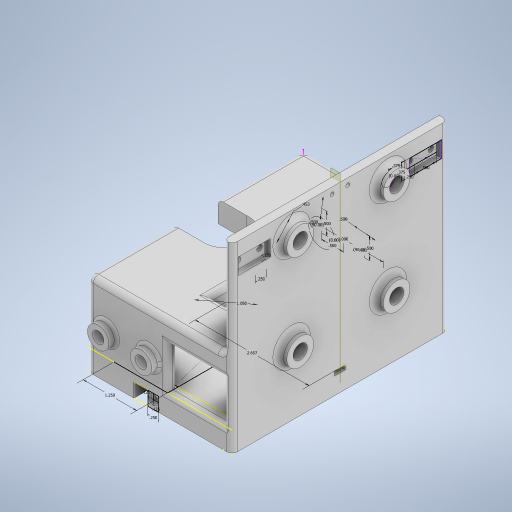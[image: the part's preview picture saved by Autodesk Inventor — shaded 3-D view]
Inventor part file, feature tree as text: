
AUTODESK INVENTOR PART (.ipt)
format: ipt  version: 2024.1 (Build 281209000, 209)  size: 974,336 bytes
history: native  units: in
note: dims shown in document units (in); Inventor stores cm internally (conversion verified against a paired STEP export)
features: extrude x22, sketch x15, hole x8, fillet x5, mirror x2, plane x1
ambient origin geometry x8: Origin, YZ Plane, XZ Plane, XY Plane, X Axis, Y Axis, Z Axis, Center Point
bodies: Solid1 (feature_tree)
feature tree (53):
  extrude  "Extrusion1"  Depth=3.3654in
  extrude  "Extrusion2"  Depth=0.375in
  extrude  "Extrusion3"  Depth=0.5in
  extrude  "Extrusion4"  Depth=4.5472in
  extrude  "Extrusion5"  Depth=0.25in
  extrude  "Extrusion6"  Depth=2.6575in
  hole  "Hole2"  [1 undecoded]
  extrude  "Extrusion7"  Depth=0.5in
  extrude  "Extrusion8"  Depth=1.5in
  extrude  "Extrusion9"  Depth=0.312in
  extrude  "Extrusion10"  Depth=0.312in
  hole  "Hole3"  [1 undecoded]
  extrude  "Extrusion11"  Depth=1.5in TaperAngle=0.0deg
  extrude  "Extrusion12"  Depth=1.125in
  hole  "Hole4"  [1 undecoded]
  sketch  "Sketch17"  dims[d34=1.4685in d35=0.0in d36=0.5in]
  extrude  "Extrusion13"  Depth=0.0625in
  hole  "Hole5"  [1 undecoded]
  plane  "Work Plane1"
  mirror  "Mirror1"
  extrude  "Extrusion14"  Depth=0.0625in
  fillet  "Fillet1"  [1 undecoded]
  extrude  "Extrusion15"  TaperAngle=0.0deg  [1 undecoded]
  fillet  "Fillet2"  Radius=0.625in
  hole  "Hole6"  [1 undecoded]
  mirror  "Mirror2"
  fillet  "Fillet3"  Radius=0.625in
  hole  "Hole7"  [1 undecoded]
  sketch  "Sketch22"  dims[d37=5.03in d38=0.0in d39=1.5in]
  extrude  "Extrusion16"  Depth=0.0625in TaperAngle=0.0deg
  fillet  "Fillet4"  Radius=0.36in
  sketch  "Sketch Driven Pattern1"  dims[d0=3.3654in d1=5.0299in]
  extrude  "Extrusion17"  Depth=0.0625in
  sketch  "Sketch24"  dims[d43=0.0in d44=0.312in]
  extrude  "Extrusion18"  Depth=0.0625in
  extrude  "Extrusion19"  Depth=0.0625in
  sketch  "Sketch26"  dims[d54=1.9685in d55=0.0in d56=1.5in d57=0.0in]
  extrude  "Extrusion20"  Depth=0.375in
  hole  "Hole8"  [1 undecoded]
  fillet  "Fillet5"  Radius=0.25in
  extrude  "Extrusion21"  Depth=0.5in
  sketch  "Sketch28"  dims[d61=1.49in d62=2.25in d63=2.25in d64=90.0deg d65=2.25in d66=90.0deg d67=0.332in d68=0.375in d69=0.119in d70=0.25in d71=0.5635in d72=0.375in d73=0.0in d74=0.0in d75=0.0in d76=0.625in d77=0.625in d78=0.625in d79=0.625in d80=0.2in d81=0.0in d82=0.36in d83=1.125in d84=0.185in d85=0.37in d86=0.09in d87=0.375in d88=0.119in d89=0.25in d90=0.5635in d91=0.375in d92=0.0in d93=0.375in d94=0.0in d95=0.25in d96=0.5in d97=0.375in d98=0.125in d99=0.0in d100=0.129in d101=0.198in d102=0.225in d103=0.188in d104=0.5635in d105=0.375in d106=0.0in d107=0.125in d108=0.125in d109=1.0in d110=1.0in d111=0.5in d112=1.5in d113=0.0in d114=0.931in d115=0.5in d116=1.0in d117=0.0in d120=0.1875in d121=0.0in d122=0.0625in d123=0.266in d124=0.75in d125=0.438in d126=0.25in d127=0.5635in d128=0.25in d129=0.0in d130=0.5in d131=90.0deg d132=0.5in d133=90.0deg d134=0.5in d135=0.5in d136=0.0625in d137=1.0in d138=0.5in d139=0.5in d140=90.0deg d141=0.5in d142=1.0in d143=180.0deg d144=1.0in d145=90.0deg d146=1.0in d147=0.266in d148=0.75in d149=0.438in d150=0.25in d151=0.5635in d152=1.0in d153=0.8108in d154=0.4532in d155=0.125in d156=0.0in d157=0.0312in d158=0.325in d159=0.1329in d160=0.3516in d161=0.1329in d162=0.3516in d163=0.448in d164=0.0in d165=0.647in d166=0.0in d167=0.325in d168=0.325in d169=0.25in d170=0.25in d171=0.5in d172=0.0in d173=0.25in d174=0.125in d175=0.0in d176=0.125in d177=0.129in d178=0.75in d179=0.219in d180=0.0625in d181=0.5635in d182=1.0in d183=0.8108in d184=0.125in d185=1.075in d186=0.325in d187=0.575in d188=0.5in d189=0.0in d190=0.25in d191=0.125in d192=0.125in d193=0.125in d194=0.0in d195=0.129in d196=0.224in d197=0.219in d198=0.0625in d199=0.5635in d200=1.0in d201=0.8108in]
  extrude  "Extrusion22"  Depth=0.375in
  hole  "Hole9"  [1 undecoded]
  sketch  "Sketch7"  dims[d3=45.0deg d4=0.375in]
  sketch  "Sketch9"  dims[d5=0.5in d6=0.0in d23=2.8543in]
  sketch  "Sketch10"  dims[d24=5.315in d25=4.5472in]
  sketch  "Sketch11"  dims[d26=0.1in d27=0.0in d28=0.25in]
  sketch  "Sketch12"  dims[d29=0.1in d30=0.0in d31=2.6575in]
  sketch  "Sketch15"  dims[d32=1.05in d33=1.25in]
  sketch  "Sketch23"  dims[d40=1.0in d41=0.0in d42=0.312in]
  sketch  "Sketch25"  dims[d45=0.196in d46=0.75in d47=0.385in d48=0.25in d49=0.5635in d50=1.378in d51=0.0in d52=1.4685in d53=0.0in]
  sketch  "Sketch27"  dims[d58=3.75in d59=0.0in d60=1.125in]
note: 10 required parameter values undecoded (feature->parameter linkage not recoverable at this tier; creation-order binding heuristic only, values carry confidence <= 0.55)
